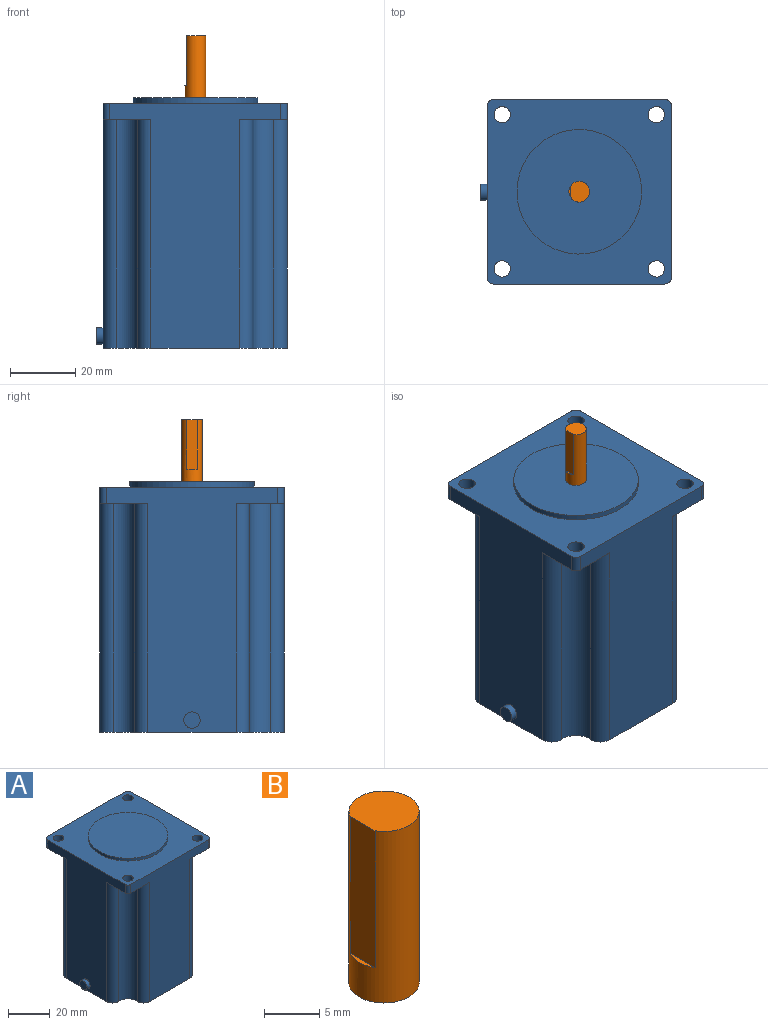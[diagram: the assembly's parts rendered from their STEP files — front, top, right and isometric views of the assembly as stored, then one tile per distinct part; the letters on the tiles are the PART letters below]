
ASSEMBLY  parts=2 mates=1
PART A: 34 faces, bbox 58.4x56.4x76.6 mm
  f0: plane 75x52.4mm, normal (-1,0,0), area 2144.9mm2, adj f2,f10,f13,f16,f17,f21,f23,f29
  f1: plane 75x52.4mm, normal (0,-1,0), area 2164.6mm2, adj f2,f3,f10,f17,f19,f21,f27,f33
  f2: plane 56.4x56.4mm, normal (0,0,-1), area 2733.1mm2, adj f0,f1,f4,f5,f18,f20,f22,f24
  f3: cylinder r=2mm len=5mm, axis (0,0,1), area 15.7mm2, adj f1,f4,f10,f19
  f4: plane 75x52.4mm, normal (1,0,0), area 2164.6mm2, adj f2,f3,f10,f15,f19,f25,f26,f31
  f5: plane 75x52.4mm, normal (0,1,0), area 2164.6mm2, adj f2,f10,f15,f16,f23,f25,f28,f30
  f6: cylinder r=2.5mm len=5mm, axis (0,0,-1), area 78.5mm2, adj f10,f23
  f7: cylinder r=2.5mm len=5mm, axis (0,0,-1), area 78.5mm2, adj f10,f21
  f8: cylinder r=2.5mm len=5mm, axis (0,0,-1), area 78.5mm2, adj f10,f25
  f9: cylinder r=2.5mm len=5mm, axis (0,0,-1), area 78.5mm2, adj f10,f19
  f10: plane 56.4x56.4mm, normal (0,0,1), area 1958.9mm2, adj f0,f1,f3,f4,f5,f6,f7,f8
  f11: cylinder r=19.05mm len=38.1mm, axis (0,0,-1), area 191.5mm2, adj f10,f12
  f12: plane 38.1x38.1mm, normal (0,0,1), area 1140.1mm2, adj f11
  f13: cylinder r=2.5mm len=5mm, axis (1,0,0), area 31.4mm2, adj f0,f14
  f14: plane 5x5mm, normal (-1,0,0), area 19.6mm2, adj f13
  f15: cylinder r=2mm len=5mm, axis (0,0,-1), area 15.7mm2, adj f4,f5,f10,f25
  f16: cylinder r=2mm len=5mm, axis (0,0,1), area 15.7mm2, adj f0,f5,f10,f23
  f17: cylinder r=2mm len=5mm, axis (0,0,-1), area 15.7mm2, adj f0,f1,f10,f21
  f18: cylinder r=6mm len=70mm, axis (0,0,-1), area 712.7mm2, adj f2,f19,f26,f27
  f19: plane 14.61x14.61mm, normal (0,0,-1), area 91.5mm2, adj f1,f3,f4,f9,f18,f26,f27
  f20: cylinder r=6mm len=70mm, axis (0,0,-1), area 712.7mm2, adj f2,f21,f32,f33
  f21: plane 14.61x14.61mm, normal (0,0,-1), area 91.5mm2, adj f0,f1,f7,f17,f20,f32,f33
  f22: cylinder r=6mm len=70mm, axis (0,0,-1), area 712.7mm2, adj f2,f23,f28,f29
  f23: plane 14.61x14.61mm, normal (0,0,-1), area 91.5mm2, adj f0,f5,f6,f16,f22,f28,f29
  f24: cylinder r=6mm len=70mm, axis (0,0,-1), area 712.7mm2, adj f2,f25,f30,f31
  f25: plane 14.61x14.61mm, normal (0,0,-1), area 91.5mm2, adj f4,f5,f8,f15,f24,f30,f31
  f26: cylinder r=4mm len=70mm, axis (0,0,-1), area 457.5mm2, adj f2,f4,f18,f19
  f27: cylinder r=4mm len=70mm, axis (0,0,-1), area 457.5mm2, adj f1,f2,f18,f19
  f28: cylinder r=4mm len=70mm, axis (0,0,-1), area 457.5mm2, adj f2,f5,f22,f23
  f29: cylinder r=4mm len=70mm, axis (0,0,-1), area 457.5mm2, adj f0,f2,f22,f23
  f30: cylinder r=4mm len=70mm, axis (0,0,-1), area 457.5mm2, adj f2,f5,f24,f25
  f31: cylinder r=4mm len=70mm, axis (0,0,-1), area 457.5mm2, adj f2,f4,f24,f25
  f32: cylinder r=4mm len=70mm, axis (0,0,-1), area 457.5mm2, adj f0,f2,f20,f21
  f33: cylinder r=4mm len=70mm, axis (0,0,-1), area 457.5mm2, adj f1,f2,f20,f21
PART B: 5 faces, bbox 6.4x6.4x19 mm
  f0: cylinder r=3.17mm len=19mm, axis (0,0,-1), area 328.4mm2, adj f1,f2,f3,f4
  f1: plane 6.35x5.92mm, normal (0,0,1), area 30.7mm2, adj f0,f3
  f2: plane 6.35x6.35mm, normal (0,0,-1), area 31.7mm2, adj f0
  f3: plane 15.15x3.19mm, normal (-1,0,0), area 48.3mm2, adj f0,f1,f4
  f4: plane 3.19x0.43mm, normal (0,0,1), area 0.9mm2, adj f0,f3
PLACE A t=(-26.55,8.87,4.16)mm
PLACE B t=(-26.55,8.87,4.16)mm
MATE revolute B.f0 <-> A.f11  axis (0,0,-1) through (-26.55,8.87,80.76)mm
